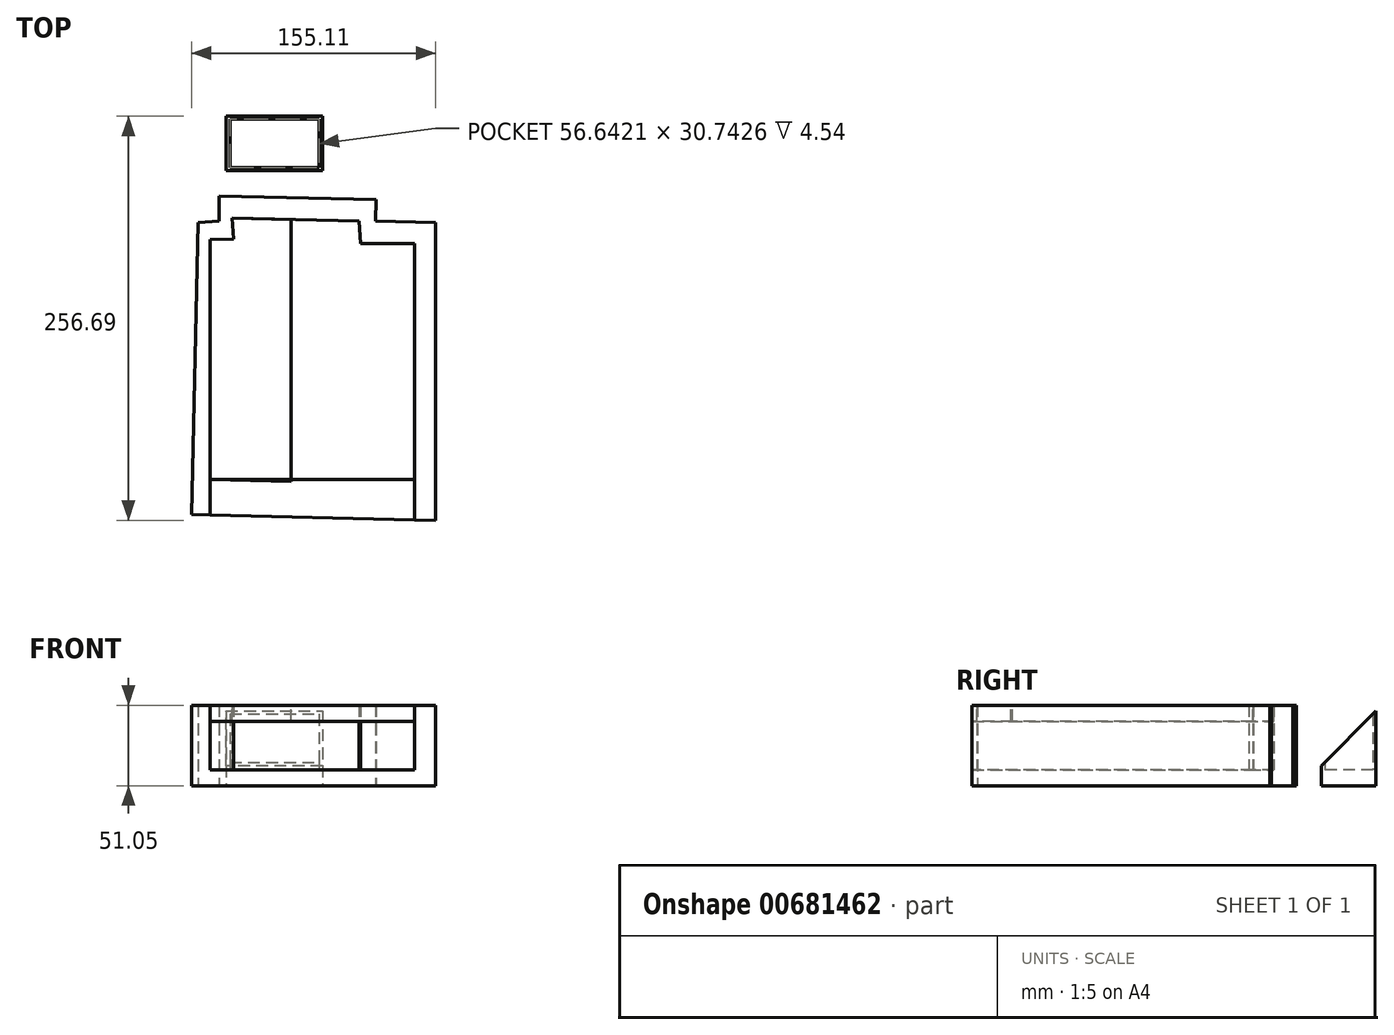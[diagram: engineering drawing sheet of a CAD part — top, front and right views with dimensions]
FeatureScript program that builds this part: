
annotation { "Feature Type Name" : "Feature", "Feature Type Description" : "" }
export const myFeature = defineFeature(function(context is Context, id is Id, definition is map)
    precondition{}
    {
        {
            var Q0;
            Q0=qCreatedBy(makeId("Top.planeOp"),FACE);
            var sketch = newSketch(context, id + "F0", { "sketchPlane" : qUnion([Q0])});
            skLineSegment(sketch, "E0", {"start": v(-48.38, -49.95) * mm, "end": v(-52.64, -235.6) * mm});
            skLineSegment(sketch, "E1", {"start": v(-52.64, -235.6) * mm, "end": v(102.47, -239.17) * mm});
            skLineSegment(sketch, "E2", {"start": v(102.47, -239.17) * mm, "end": v(102.47, -49.95) * mm});
            skLineSegment(sketch, "E3", {"start": v(102.47, -49.95) * mm, "end": v(64.3, -49.08) * mm});
            skLineSegment(sketch, "E4", {"start": v(64.3, -49.08) * mm, "end": v(64.62, -35.4) * mm});
            skLineSegment(sketch, "E5", {"start": v(64.62, -35.4) * mm, "end": v(-35.2, -33.11) * mm});
            skLineSegment(sketch, "E6", {"start": v(-35.2, -33.11) * mm, "end": v(-35.2, -49.08) * mm});
            skLineSegment(sketch, "E7", {"start": v(-35.2, -49.08) * mm, "end": v(-48.38, -49.95) * mm});
            skLineSegment(sketch, "E8", {"start": v(-40.63, -60.85) * mm, "end": v(-40.63, -235.88) * mm});
            skLineSegment(sketch, "E9", {"start": v(-40.63, -235.88) * mm, "end": v(89.06, -238.86) * mm});
            skLineSegment(sketch, "E10", {"start": v(89.06, -238.86) * mm, "end": v(89.06, -63.23) * mm});
            skLineSegment(sketch, "E11", {"start": v(89.06, -63.23) * mm, "end": v(54.73, -63.23) * mm});
            skLineSegment(sketch, "E12", {"start": v(54.73, -63.23) * mm, "end": v(53.8, -49.08) * mm});
            skLineSegment(sketch, "E13", {"start": v(53.8, -49.08) * mm, "end": v(-26.84, -47.23) * mm});
            skLineSegment(sketch, "E14", {"start": v(-26.84, -47.23) * mm, "end": v(-25.96, -60.4) * mm});
            skLineSegment(sketch, "E15", {"start": v(-25.96, -60.4) * mm, "end": v(-40.63, -60.85) * mm});
            skSolve(sketch);
        }
        {
            var Q0;
            {var subQ1=sQuery(id+"F0.wireOp",EDGE,"E0");Q0=makeQuery(id+"F0.imprint","IMPRINT",FACE,{"disambiguationData":[TD([[makeQuery(id+"F0.imprint","IMPRINT",EDGE,{"derivedFrom":subQ1}),1.0]])]});}
            extrude(context, id + "F1", {"entities" : qUnion([Q0]), "depth" : 51.05 * mm, "offsetDistance" : 25.4 * mm});
        }
        {
            var Q0;
            Q0=makeQuery(id+"F0.imprint","IMPRINT",FACE,{"disambiguationData":[TD([[makeQuery(id+"F0.imprint","IMPRINT",EDGE,{"derivedFrom":sQuery(id+"F0.wireOp",EDGE,"E8")}),1.0]])]});
            extrude(context, id + "F2", {"entities" : qUnion([Q0]), "operationType" : NewBodyOperationType.ADD, "depth" : 10.16 * mm, "offsetDistance" : 25.4 * mm});
        }
        {
            var Q0;
            Q0=makeQuery(id+"F1.opExtrude","CAP_FACE",FACE,{"disambiguationData":[OSD([sQuery(id+"F0.wireOp",EDGE,"E0"),sQuery(id+"F0.wireOp",EDGE,"E1"),sQuery(id+"F0.wireOp",EDGE,"E2"),sQuery(id+"F0.wireOp",EDGE,"E3"),sQuery(id+"F0.wireOp",EDGE,"E4"),sQuery(id+"F0.wireOp",EDGE,"E5"),sQuery(id+"F0.wireOp",EDGE,"E6"),sQuery(id+"F0.wireOp",EDGE,"E7"),sQuery(id+"F0.wireOp",EDGE,"E8"),sQuery(id+"F0.wireOp",EDGE,"E10"),sQuery(id+"F0.wireOp",EDGE,"E11"),sQuery(id+"F0.wireOp",EDGE,"E12"),sQuery(id+"F0.wireOp",EDGE,"E13"),sQuery(id+"F0.wireOp",EDGE,"E14"),sQuery(id+"F0.wireOp",EDGE,"E15")])],"isStart":false});
            var sketch = newSketch(context, id + "F3", { "sketchPlane" : qUnion([Q0])});
            skLineSegment(sketch, "E16", {"start": v(-52.64, -235.6) * mm, "end": v(102.47, -239.17) * mm});
            skLineSegment(sketch, "E17", {"start": v(102.47, -239.17) * mm, "end": v(102.47, -213.33) * mm});
            skLineSegment(sketch, "E18", {"start": v(102.47, -213.33) * mm, "end": v(-52.13, -213.33) * mm});
            skLineSegment(sketch, "E19", {"start": v(-52.13, -213.33) * mm, "end": v(-52.64, -235.6) * mm});
            skSolve(sketch);
        }
        {
            var Q0;
            {var subQ0=sQuery(id+"F3.wireOp",EDGE,"E16");var subQ1=makeQuery(id+"F1.opExtrude","CAP_EDGE",EDGE,{"disambiguationData":[OSD([sQuery(id+"F0.wireOp",EDGE,"E8")])],"isStart":false});var subQ2=makeQuery(id+"F3.imprint","INTERSECT",VERTEX,{"derivedFrom":[subQ1,subQ0]});Q0=makeQuery(id+"F3.imprint","IMPRINT",FACE,{"disambiguationData":[TD([[makeQuery(id+"F3.imprint","IMPRINT",EDGE,{"disambiguationData":[TD([[subQ2,-1.0]])],"derivedFrom":subQ0}),1.0]])]});}
            extrude(context, id + "F4", {"entities" : qUnion([Q0]), "oppositeDirection" : true, "depth" : 10.16 * mm, "offsetDistance" : 25.4 * mm});
        }
        {
            var Q0;
            Q0=makeQuery(id+"F1.opExtrude","CAP_FACE",FACE,{"disambiguationData":[OSD([sQuery(id+"F0.wireOp",EDGE,"E0"),sQuery(id+"F0.wireOp",EDGE,"E1"),sQuery(id+"F0.wireOp",EDGE,"E2"),sQuery(id+"F0.wireOp",EDGE,"E3"),sQuery(id+"F0.wireOp",EDGE,"E4"),sQuery(id+"F0.wireOp",EDGE,"E5"),sQuery(id+"F0.wireOp",EDGE,"E6"),sQuery(id+"F0.wireOp",EDGE,"E7"),sQuery(id+"F0.wireOp",EDGE,"E8"),sQuery(id+"F0.wireOp",EDGE,"E10"),sQuery(id+"F0.wireOp",EDGE,"E11"),sQuery(id+"F0.wireOp",EDGE,"E12"),sQuery(id+"F0.wireOp",EDGE,"E13"),sQuery(id+"F0.wireOp",EDGE,"E14"),sQuery(id+"F0.wireOp",EDGE,"E15")])],"isStart":false});
            var sketch = newSketch(context, id + "F5", { "sketchPlane" : qUnion([Q0])});
            skLineSegment(sketch, "E20", {"start": v(-40.63, -213.33) * mm, "end": v(10.55, -214.5) * mm});
            skLineSegment(sketch, "E21", {"start": v(10.55, -214.5) * mm, "end": v(10.55, -48.08) * mm});
            skLineSegment(sketch, "E22", {"start": v(10.55, -48.08) * mm, "end": v(-26.84, -47.23) * mm});
            skLineSegment(sketch, "E23", {"start": v(-26.84, -47.23) * mm, "end": v(-25.96, -60.4) * mm});
            skLineSegment(sketch, "E24", {"start": v(-25.96, -60.4) * mm, "end": v(-40.63, -60.85) * mm});
            skLineSegment(sketch, "E25", {"start": v(-40.63, -60.85) * mm, "end": v(-40.63, -213.33) * mm});
            skSolve(sketch);
        }
        {
            var Q0;
            Q0=makeQuery(id+"F5.imprint","IMPRINT",FACE,{"disambiguationData":[TD([[makeQuery(id+"F5.imprint","IMPRINT",EDGE,{"derivedFrom":sQuery(id+"F5.wireOp",EDGE,"E20")}),1.0]])]});
            extrude(context, id + "F6", {"entities" : qUnion([Q0]), "oppositeDirection" : true, "depth" : 10.16 * mm, "offsetDistance" : 25.4 * mm});
        }
        {
            var Q0;
            Q0=qCreatedBy(makeId("Top.planeOp"),FACE);
            var sketch = newSketch(context, id + "F7", { "sketchPlane" : qUnion([Q0])});
            skLineSegment(sketch, "E26.bottom", {"start": v(-30.68, 17.52) * mm, "end": v(30.6, 17.52) * mm});
            skLineSegment(sketch, "E26.top", {"start": v(-30.68, -17.12) * mm, "end": v(30.6, -17.12) * mm});
            skLineSegment(sketch, "E26.left", {"start": v(-30.68, 17.52) * mm, "end": v(-30.68, -17.12) * mm});
            skLineSegment(sketch, "E26.right", {"start": v(30.6, 17.52) * mm, "end": v(30.6, -17.12) * mm});
            skLineSegment(sketch, "E27.bottom", {"start": v(-28.15, 15.63) * mm, "end": v(28.49, 15.63) * mm});
            skLineSegment(sketch, "E27.top", {"start": v(-28.15, -15.12) * mm, "end": v(28.49, -15.12) * mm});
            skLineSegment(sketch, "E27.left", {"start": v(-28.15, 15.63) * mm, "end": v(-28.15, -15.12) * mm});
            skLineSegment(sketch, "E27.right", {"start": v(28.49, 15.63) * mm, "end": v(28.49, -15.12) * mm});
            skSolve(sketch);
        }
        {
            var Q0;
            Q0=makeQuery(id+"F7.imprint","IMPRINT",FACE,{"disambiguationData":[TD([[makeQuery(id+"F7.imprint","IMPRINT",EDGE,{"derivedFrom":sQuery(id+"F7.wireOp",EDGE,"E27.bottom")}),-1.0]])]});
            extrude(context, id + "F8", {"entities" : qUnion([Q0]), "depth" : 10.16 * mm, "offsetDistance" : 25.4 * mm});
        }
        {
            var Q0;
            Q0=makeQuery(id+"F7.imprint","IMPRINT",FACE,{"disambiguationData":[TD([[makeQuery(id+"F7.imprint","IMPRINT",EDGE,{"derivedFrom":sQuery(id+"F7.wireOp",EDGE,"E26.bottom")}),-1.0]])]});
            extrude(context, id + "F9", {"entities" : qUnion([Q0]), "operationType" : NewBodyOperationType.ADD, "depth" : 63.5 * mm, "offsetDistance" : 25.4 * mm});
        }
        {
            var Q0;
            Q0=makeQuery(id+"F9.opExtrude","CAP_EDGE",EDGE,{"disambiguationData":[OSD([sQuery(id+"F7.wireOp",EDGE,"E26.top")])],"isStart":false});
            chamfer(context, id + "F10", {"entities" : qUnion([Q0]), "width" : 50.8 * mm, "tangentPropagation" : true});
        }
    });
